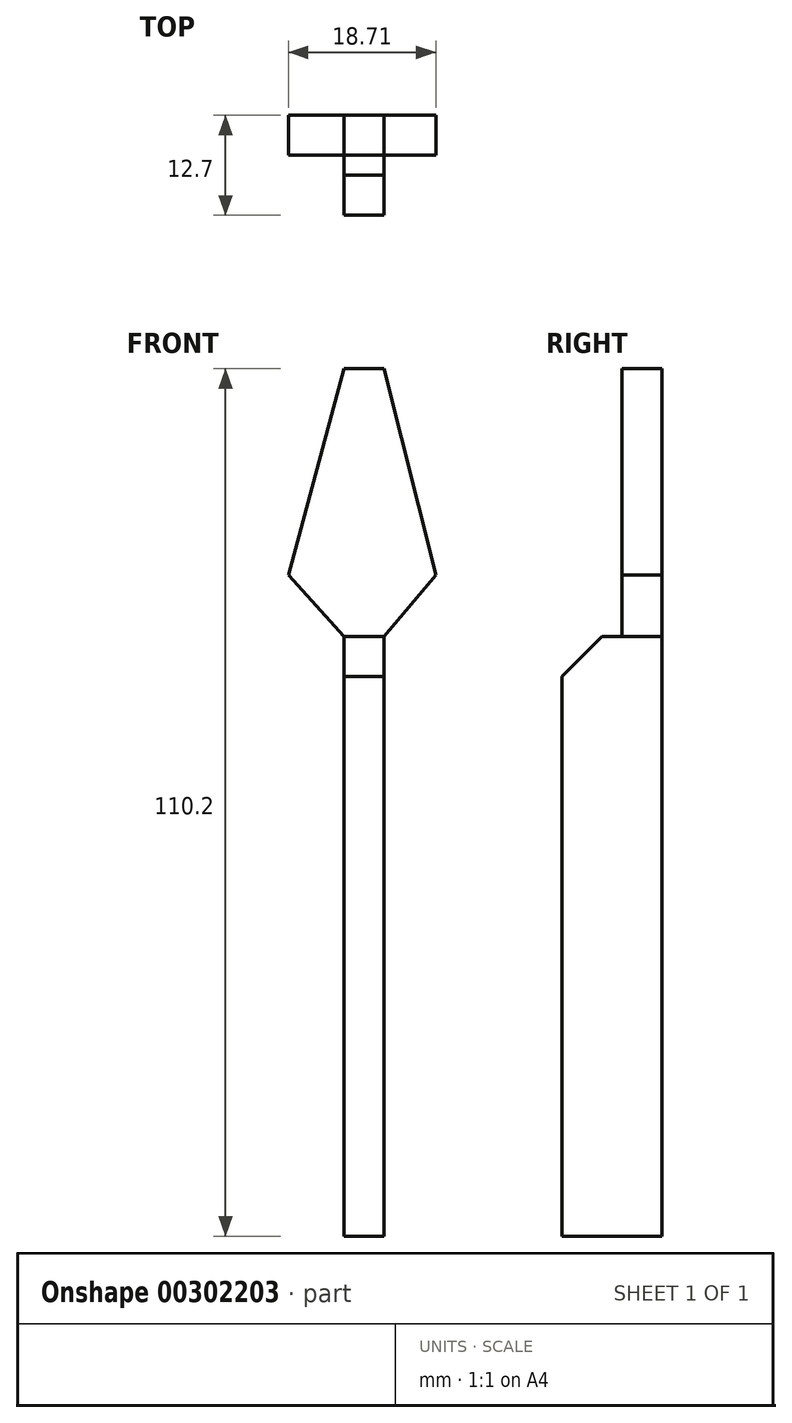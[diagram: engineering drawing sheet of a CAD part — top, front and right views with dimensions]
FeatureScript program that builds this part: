
annotation { "Feature Type Name" : "Feature", "Feature Type Description" : "" }
export const myFeature = defineFeature(function(context is Context, id is Id, definition is map)
    precondition{}
    {
        {
            var Q0;
            Q0=qCreatedBy(makeId("Front.planeOp"),FACE);
            var sketch = newSketch(context, id + "F0", { "sketchPlane" : qUnion([Q0])});
            skLineSegment(sketch, "E0", {"start": v(-45.32, 35.65) * mm, "end": v(-45.32, -40.55) * mm});
            skLineSegment(sketch, "E1", {"start": v(-40.24, 35.65) * mm, "end": v(-40.24, -40.55) * mm});
            skLineSegment(sketch, "E2", {"start": v(-45.32, 35.65) * mm, "end": v(-40.24, 35.65) * mm});
            skLineSegment(sketch, "E3", {"start": v(-45.32, 35.65) * mm, "end": v(-52.38, 43.46) * mm});
            skLineSegment(sketch, "E4", {"start": v(-40.24, 35.65) * mm, "end": v(-33.67, 43.46) * mm});
            skLineSegment(sketch, "E5", {"start": v(-52.38, 43.46) * mm, "end": v(-45.32, 69.65) * mm});
            skLineSegment(sketch, "E6", {"start": v(-33.67, 43.46) * mm, "end": v(-40.24, 69.65) * mm});
            skLineSegment(sketch, "E7", {"start": v(-45.32, 69.65) * mm, "end": v(-40.24, 69.65) * mm});
            skLineSegment(sketch, "E8", {"start": v(-45.32, -40.55) * mm, "end": v(-40.24, -40.55) * mm});
            skSolve(sketch);
        }
        {
            var Q0;
            Q0=makeQuery(id+"F0.imprint","IMPRINT",FACE,{"disambiguationData":[TD([[makeQuery(id+"F0.imprint","IMPRINT",EDGE,{"derivedFrom":sQuery(id+"F0.wireOp",EDGE,"E0")}),1.0]])]});
            extrude(context, id + "F1", {"entities" : qUnion([Q0]), "depth" : 12.7 * mm});
        }
        {
            var Q0;
            Q0 = qSketchRegion(id + "F0", true);
            extrude(context, id + "F2", {"entities" : qUnion([Q0]), "operationType" : NewBodyOperationType.ADD, "depth" : 5.08 * mm});
        }
        {
            var Q0;
            Q0=makeQuery(id+"F1.opExtrude","CAP_EDGE",EDGE,{"disambiguationData":[OSD([sQuery(id+"F0.wireOp",EDGE,"E2")])],"isStart":false});
            chamfer(context, id + "F3", {"entities" : qUnion([Q0]), "width" : 5.08 * mm, "tangentPropagation" : true});
        }
    });
